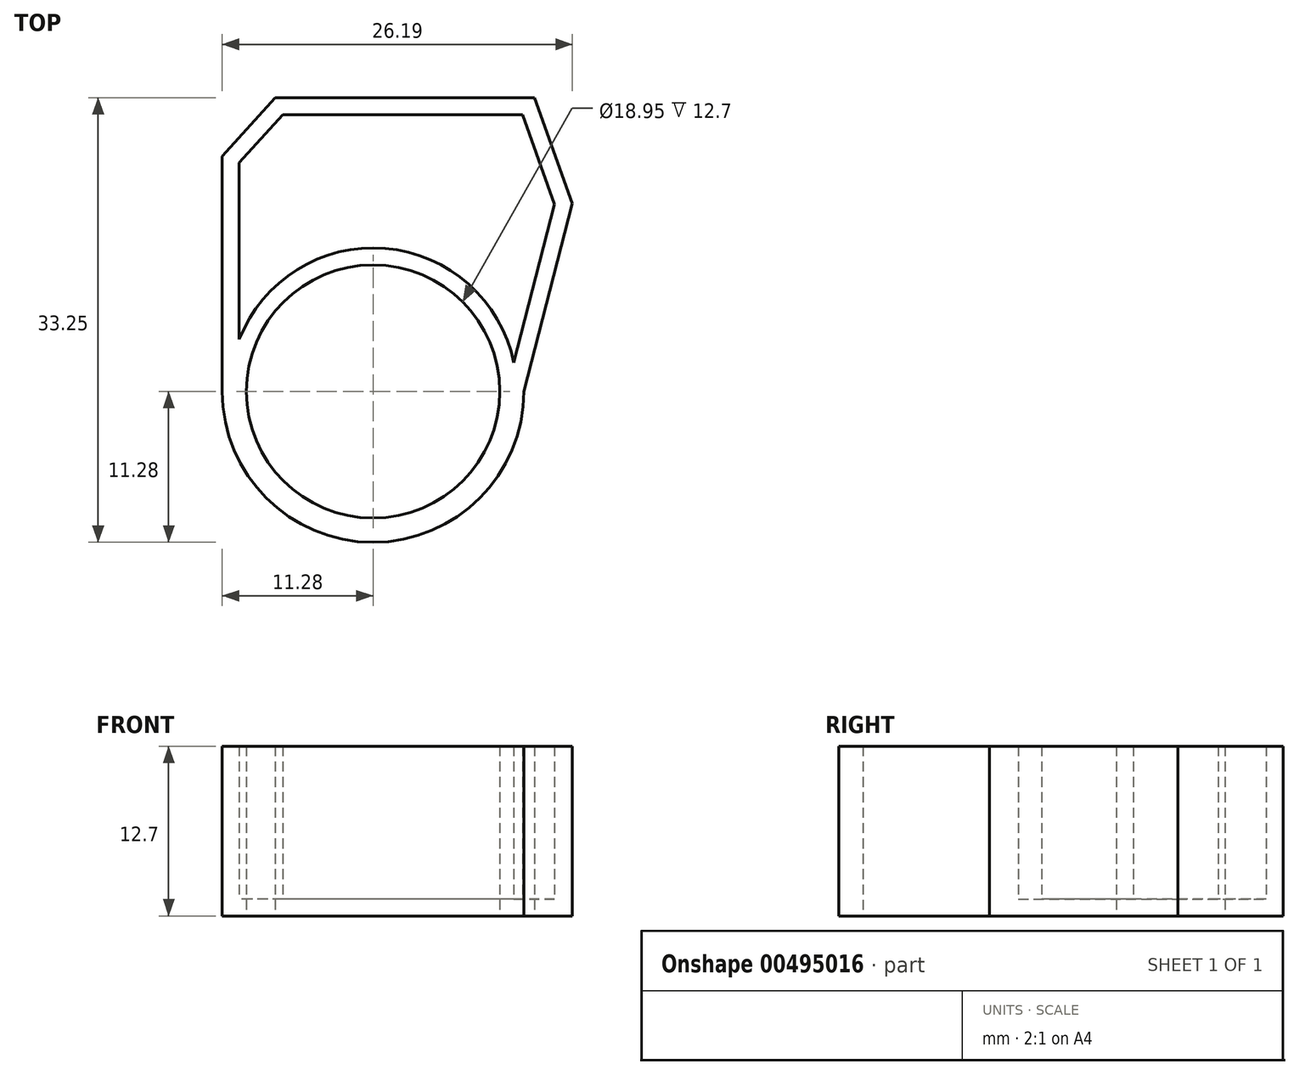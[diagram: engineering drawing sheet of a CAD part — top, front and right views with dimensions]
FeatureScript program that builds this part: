
annotation { "Feature Type Name" : "Feature", "Feature Type Description" : "" }
export const myFeature = defineFeature(function(context is Context, id is Id, definition is map)
    precondition{}
    {
        {
            var Q0;
            Q0=qCreatedBy(makeId("Top.planeOp"),FACE);
            var sketch = newSketch(context, id + "F0", { "sketchPlane" : qUnion([Q0])});
            skCircle(sketch, "E0", {"center": v(0, 0) * mm, "radius": 9.47 * mm});
            skArc(sketch, "E1", {"start": v(-11.28, 0) * mm, "mid": v(0, -11.28) * mm, "end": v(11.28, 0) * mm});
            skLineSegment(sketch, "E2", {"start": v(11.28, 0) * mm, "end": v(14.9, 14.07) * mm});
            skLineSegment(sketch, "E3", {"start": v(14.9, 14.07) * mm, "end": v(12.07, 21.97) * mm});
            skLineSegment(sketch, "E4", {"start": v(12.07, 21.97) * mm, "end": v(-7.33, 21.97) * mm});
            skLineSegment(sketch, "E5", {"start": v(-7.33, 21.97) * mm, "end": v(-11.28, 17.6) * mm});
            skLineSegment(sketch, "E6", {"start": v(-11.28, 17.6) * mm, "end": v(-11.28, 0) * mm});
            skSolve(sketch);
        }
        {
            var Q0;
            Q0=makeQuery(id+"F0.imprint","IMPRINT",FACE,{"disambiguationData":[TD([[makeQuery(id+"F0.imprint","IMPRINT",EDGE,{"derivedFrom":sQuery(id+"F0.wireOp",EDGE,"E0")}),-1.0]])]});
            extrude(context, id + "F1", {"entities" : qUnion([Q0]), "depth" : 12.7 * mm, "offsetDistance" : 25.4 * mm});
        }
        {
            var Q0;
            Q0=makeQuery(id+"F1.opExtrude","CAP_FACE",FACE,{"disambiguationData":[OSD([sQuery(id+"F0.wireOp",EDGE,"E0"),sQuery(id+"F0.wireOp",EDGE,"E1"),sQuery(id+"F0.wireOp",EDGE,"E2"),sQuery(id+"F0.wireOp",EDGE,"E3"),sQuery(id+"F0.wireOp",EDGE,"E4"),sQuery(id+"F0.wireOp",EDGE,"E5"),sQuery(id+"F0.wireOp",EDGE,"E6")])],"isStart":false});
            shell(context, id + "F2", {"entities" : qUnion([Q0]), "thickness" : 1.27 * mm});
        }
    });
